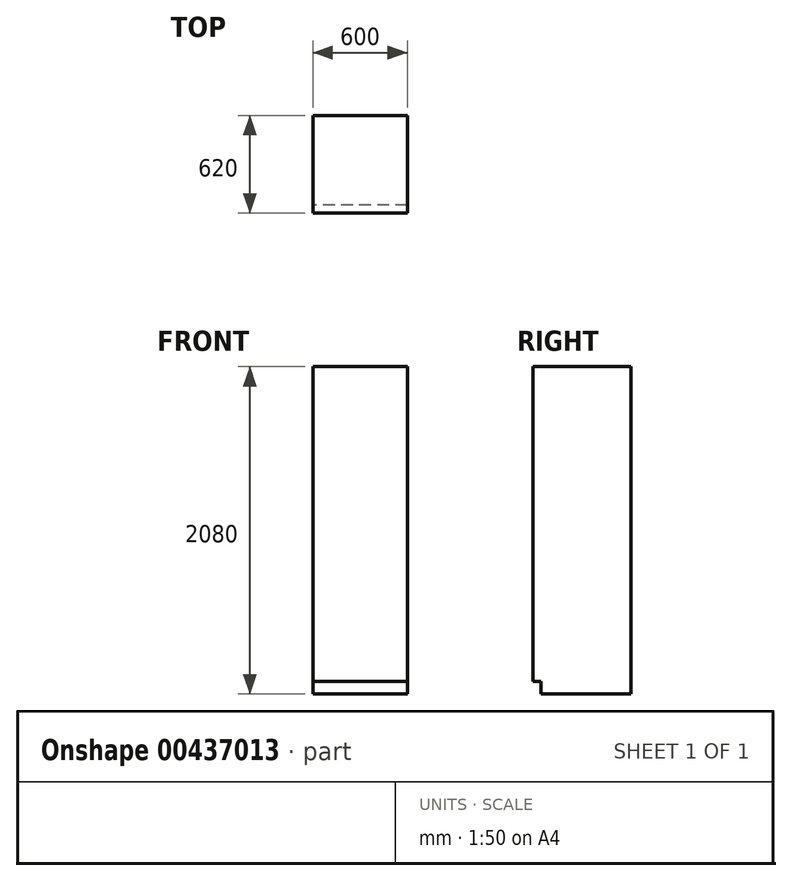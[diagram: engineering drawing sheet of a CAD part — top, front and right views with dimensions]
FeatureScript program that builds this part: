
annotation { "Feature Type Name" : "Feature", "Feature Type Description" : "" }
export const myFeature = defineFeature(function(context is Context, id is Id, definition is map)
    precondition{}
    {
        {
            var Q0;
            Q0=qCreatedBy(makeId("Right.planeOp"),FACE);
            var sketch = newSketch(context, id + "F0", { "sketchPlane" : qUnion([Q0])});
            skLineSegment(sketch, "E0.bottom", {"start": v(0, 0) * mm, "end": v(-570, 0) * mm});
            skLineSegment(sketch, "E0.top", {"start": v(0, 2080) * mm, "end": v(-620, 2080) * mm});
            skLineSegment(sketch, "E0.left", {"start": v(0, 0) * mm, "end": v(0, 2080) * mm});
            skLineSegment(sketch, "E0.right", {"start": v(-620, 80) * mm, "end": v(-620, 2080) * mm});
            skLineSegment(sketch, "E1.top", {"start": v(-620, 80) * mm, "end": v(-570, 80) * mm});
            skLineSegment(sketch, "E1.right", {"start": v(-570, 0) * mm, "end": v(-570, 80) * mm});
            skSolve(sketch);
        }
        {
            var Q0;
            Q0 = qSketchRegion(id + "F0", true);
            extrude(context, id + "F1", {"entities" : qUnion([Q0]), "depth" : 600 * mm});
        }
    });
